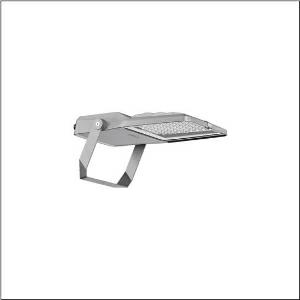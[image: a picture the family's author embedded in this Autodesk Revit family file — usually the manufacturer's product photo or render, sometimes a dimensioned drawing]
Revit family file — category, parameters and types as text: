
# Revit family: floodlight_fl_21_mini___rs12_5xa7772c3b1a_5444
name_source: partatom
category: Lighting Fixtures
units: mm (PartAtom-declared; Revit-internal decimal feet)

## family parameters
Cut with Voids When Loaded = No
Host = Face
Light Source = No
Part Type = Normal
Room Calculation Point = No
Round Connector Dimension = Use Diameter
Shared = No

## types (1)
- --- (1 x LED, 10620 lm, 87.2 W, 3000K)
    Apparent Load = 87 VA
    CIE Flux Codes = 79 92 99 100 100
    Color Rendering = 80
    Color Temperature = 3000K
    Default Elevation = 1800 mm
    Description = Floodlight FL 21 mini, floodlight, primary light control with lens, of PMMA, primary optical cover: protective disc, of toughened safety glass, transparent, light distribution: RS12, light emission: direct distribution, installation type: surface-mounted, LED, High Power LED, rated luminous flux: 10.620lm, luminous efficacy: 122lm/W, light colour: 830, colour temperature: 3000K, control gear: ECG iQ, control: Street-Remote, Auto-Match, Temp-Guard, Night-Set, Smart-Wire, Desk-Remote (wireless, voltage-free reading and setting of iQ features in the workshop via application-optimized NFC function/RFID function), optimised constant luminous flux control (CLO 2.0), with terminal, 6-pole, mains connection: 220..240V, AC, 50/60Hz, start of lifetime: 87W, end of lifetime: 92W, reduction: 40W, luminaire housing, of diecast aluminium, powder-coated, Siteco® metallic grey (DB 702S), corrosivity category C5 according to DIN EN ISO 12944, mounting bracket, of steel, galvanised, powder-coated, Siteco® metallic grey (DB 702S), protection rating (complete): IP66, insulation class (complete): insulation class II (safety insulation), certification: CE, ENEC, VDE, protection symbol: D, impact resistance: IK08, permissible operating ambient temperature: -40..+40°C, permissible operating ambient temperature for outdoor applications: -40..+50°C, standard: DIN EN 12944, packaging unit: 1 piece

Light Distribution: RS12
    Height = 70 mm
    Lamp = 1 x LED
    Lamp Light Flux = 10620 lm
    Lamp Power = 87.2 W
    Lamp count = 1
    Length = 485 mm
    Luminous efficacy = 122 lm/W
    Manufacturer = Siteco
    ModVariant = No
    Model = 5XA7772C3B1A
    Number of Poles = 1
    OnlyDefault = Yes
    Power Factor = 1
    Product Name = Floodlight FL 21 mini | RS12
    Product group = floodlight | pylon top
    ProductGroupID = 6101
    Protection Class = Protection class II
    Protection Degree = IP 66
    RLX_Detail_Level = 1
    RlxData = <blob elided: 90845 chars, md5=50b61e41>
    Socket = socket
    Standby Power = 0 W
    System Light Flux = 10620 lm
    System Power = 87 W
    Type Comments = factory setting: luminous flux: 100 % | dim-lin: 254 | 456 mA
    Type Image = l_1006845.jpg
    URL = http://relux.com
    VarID = @adj_078667
    Voltage = 0 V
    Weight = 0.00 kg
    Width = 337 mm

## geometry (parser evidence)
native form markers: Blend x4, Sweep x12
no freeform markers — native parametric forms only
